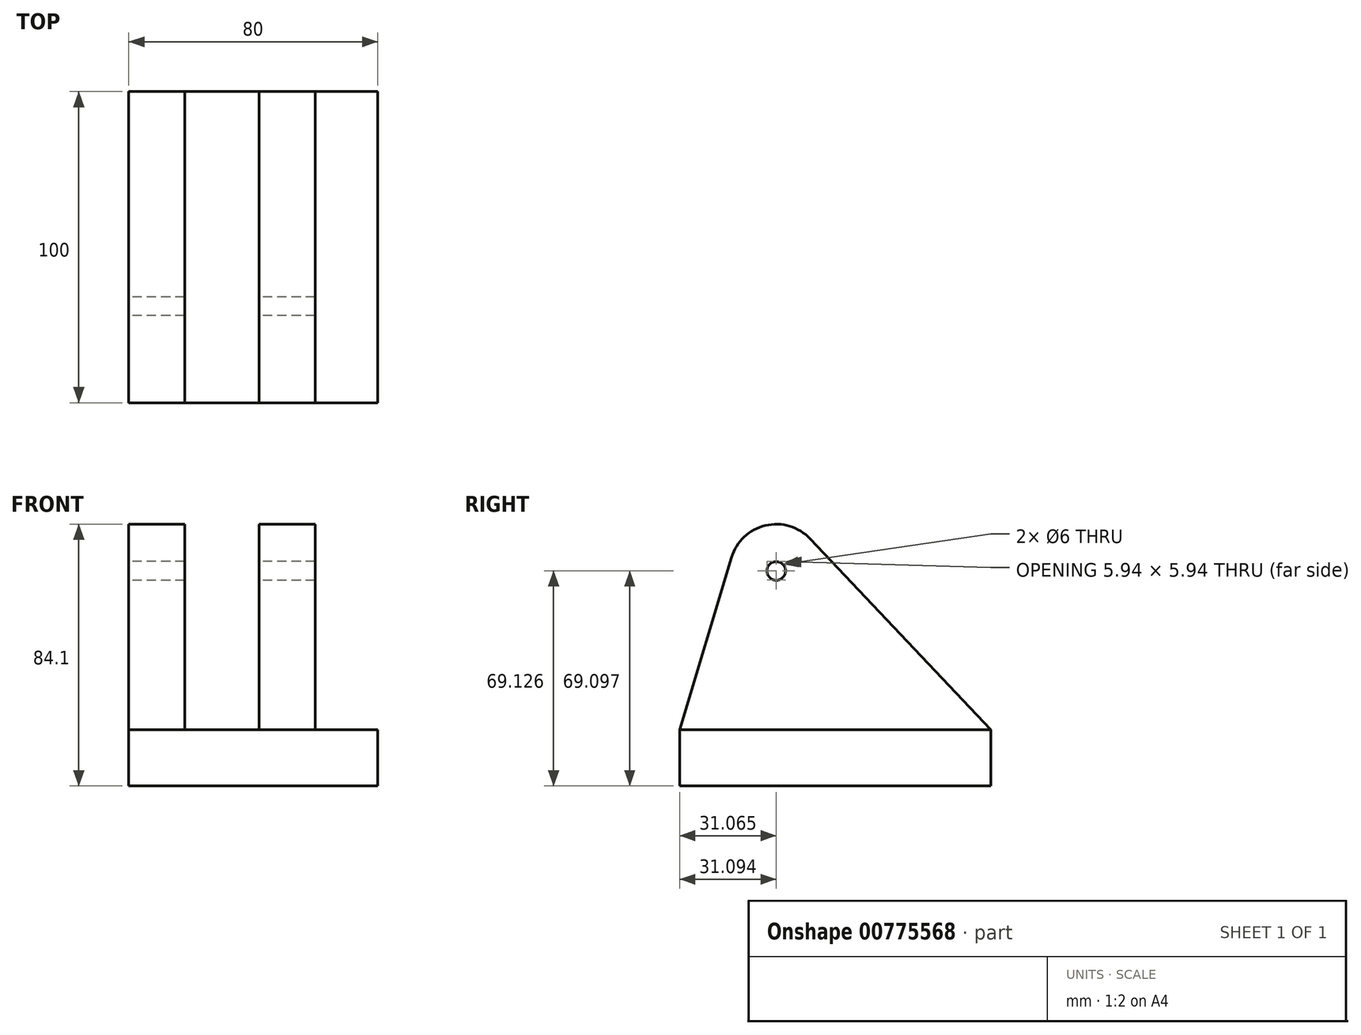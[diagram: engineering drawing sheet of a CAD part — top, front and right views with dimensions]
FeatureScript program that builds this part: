
annotation { "Feature Type Name" : "Feature", "Feature Type Description" : "" }
export const myFeature = defineFeature(function(context is Context, id is Id, definition is map)
    precondition{}
    {
        {
            var Q0;
            Q0=qCreatedBy(makeId("Top.planeOp"),FACE);
            var sketch = newSketch(context, id + "F0", { "sketchPlane" : qUnion([Q0])});
            skLineSegment(sketch, "E0.bottom", {"start": v(-45.05, 38.96) * mm, "end": v(34.95, 38.96) * mm});
            skLineSegment(sketch, "E0.top", {"start": v(-45.05, -61.04) * mm, "end": v(34.95, -61.04) * mm});
            skLineSegment(sketch, "E0.left", {"start": v(-45.05, 38.96) * mm, "end": v(-45.05, -61.04) * mm});
            skLineSegment(sketch, "E0.right", {"start": v(34.95, 38.96) * mm, "end": v(34.95, -61.04) * mm});
            skSolve(sketch);
        }
        {
            var Q0;
            Q0=makeQuery(id+"F0.imprint","IMPRINT",FACE,{"disambiguationData":[TD([[makeQuery(id+"F0.imprint","IMPRINT",EDGE,{"derivedFrom":sQuery(id+"F0.wireOp",EDGE,"E0.bottom")}),-1.0]])]});
            extrude(context, id + "F1", {"entities" : qUnion([Q0]), "depth" : 18 * mm, "offsetDistance" : 25 * mm});
        }
        {
            var Q0;
            Q0=makeQuery(id+"F1.opExtrude","CAP_FACE",FACE,{"disambiguationData":[OSD([sQuery(id+"F0.wireOp",EDGE,"E0.bottom"),sQuery(id+"F0.wireOp",EDGE,"E0.top"),sQuery(id+"F0.wireOp",EDGE,"E0.left"),sQuery(id+"F0.wireOp",EDGE,"E0.right")])],"isStart":false});
            var sketch = newSketch(context, id + "F2", { "sketchPlane" : qUnion([Q0])});
            skLineSegment(sketch, "E1.bottom", {"start": v(-45.05, 38.96) * mm, "end": v(-27.05, 38.96) * mm});
            skLineSegment(sketch, "E1.top", {"start": v(-45.05, -61.04) * mm, "end": v(-27.05, -61.04) * mm});
            skLineSegment(sketch, "E1.left", {"start": v(-45.05, 38.96) * mm, "end": v(-45.05, -61.04) * mm});
            skLineSegment(sketch, "E1.right", {"start": v(-27.05, 38.96) * mm, "end": v(-27.05, -61.04) * mm});
            skSolve(sketch);
        }
        {
            var Q0;
            Q0=makeQuery(id+"F2.imprint","IMPRINT",FACE,{"disambiguationData":[TD([[makeQuery(id+"F2.imprint","IMPRINT",EDGE,{"derivedFrom":sQuery(id+"F2.wireOp",EDGE,"E1.bottom")}),-1.0]])]});
            extrude(context, id + "F3", {"entities" : qUnion([Q0]), "depth" : 70 * mm, "offsetDistance" : 25 * mm});
        }
        {
            var Q0;
            Q0=makeQuery(id+"F3.opExtrude","SWEPT_FACE",FACE,{"disambiguationData":[OSD([sQuery(id+"F2.wireOp",EDGE,"E1.left")])]});
            var sketch = newSketch(context, id + "F4", { "sketchPlane" : qUnion([Q0])});
            skArc(sketch, "E2", {"start": v(44.34, 73.43) * mm, "mid": v(33.43, 83.7) * mm, "end": v(19.07, 79.4) * mm});
            skLineSegment(sketch, "E3", {"start": v(61.04, 18) * mm, "end": v(44.34, 73.43) * mm});
            skLineSegment(sketch, "E4", {"start": v(-38.96, 18) * mm, "end": v(19.07, 79.4) * mm});
            skSolve(sketch);
        }
        {
            var Q0;
            Q0=makeQuery(id+"F4.imprint","IMPRINT",FACE,{"disambiguationData":[TD([[makeQuery(id+"F4.imprint","IMPRINT",EDGE,{"derivedFrom":sQuery(id+"F4.wireOp",EDGE,"E2")}),-1.0]])]});
            extrude(context, id + "F5", {"entities" : qUnion([Q0]), "operationType" : NewBodyOperationType.REMOVE, "oppositeDirection" : true, "depth" : 25 * mm, "offsetDistance" : 25 * mm});
        }
        {
            var Q0;
            Q0=sQuery(id+"F4.wireOp",VERTEX,"E2.center");
            var Q1;
            Q1=makeQuery(id+"F3.opExtrude","SWEPT_BODY",BODY,{"disambiguationData":[OSD([sQuery(id+"F2.wireOp",EDGE,"E1.bottom"),sQuery(id+"F2.wireOp",EDGE,"E1.top"),sQuery(id+"F2.wireOp",EDGE,"E1.left"),sQuery(id+"F2.wireOp",EDGE,"E1.right")])]});
            hole(context, id + "F6", {"style" : HoleStyle.SIMPLE, "endStyle" : HoleEndStyle.THROUGH, "holeDiameter" : 6 * mm, "majorDiameter" : 5 * mm, "isTappedThrough" : true, "tappedDepth" : 12 * mm, "tapClearance" : 3, "locations" : qUnion([Q0]), "scope" : qUnion([Q1])});
        }
        {
            var Q0;
            Q0=makeQuery(id+"F3.opExtrude","SWEPT_BODY",BODY,{"disambiguationData":[OSD([sQuery(id+"F2.wireOp",EDGE,"E1.bottom"),sQuery(id+"F2.wireOp",EDGE,"E1.top"),sQuery(id+"F2.wireOp",EDGE,"E1.left"),sQuery(id+"F2.wireOp",EDGE,"E1.right")])]});
            transform(context, id + "F7", {"entities" : qUnion([Q0]), "transformType" : TransformType.TRANSLATION_3D, "dx" : 41.9 * mm, "dy" : 0 * mm, "dz" : 0 * mm, "makeCopy" : true});
        }
    });
